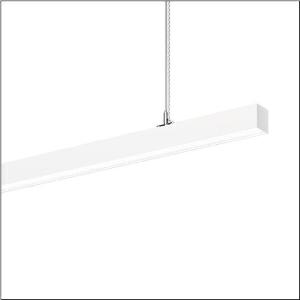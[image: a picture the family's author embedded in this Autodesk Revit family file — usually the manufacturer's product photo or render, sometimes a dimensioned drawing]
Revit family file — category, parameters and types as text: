
# Revit family: silica_r__21_51mx33tctdw_01d4
name_source: partatom
category: Lighting Fixtures
units: mm (PartAtom-declared; Revit-internal decimal feet)

## family parameters
Cut with Voids When Loaded = No
Host = Face
Light Source = No
Part Type = Normal
Room Calculation Point = No
Round Connector Dimension = Use Diameter
Shared = No

## types (1)
- --- (1 x LED, 14340 lm, 134.7 W, 6500K)
    Apparent Load = 135 VA
    CIE Flux Codes = 78 96 99 56 100
    Color Rendering = 80
    Color Temperature = 6500K
    Default Elevation = 1800 mm
    Description = Silica® 21, office luminaire, primary optical cover: prismatic diffuser, of PMMA, CAT 2 (L<= 3000cd/m²), light emission: direct/indirect distribution, primary light characteristic: symmetric, installation type: suspended mounting, LED, rated luminous flux: 14.340lm, luminous efficacy: 101lm/W, light colour: 8tw, colour temperature: 2700..6500K, control gear: ECG DALI, with terminal, 3+2-pole, max. 2.5mm², mains connection: 220..240V, AC, 50/60Hz, rated input power: 141.4W, luminaire housing, of aluminium, traffic white (RAL 9016), length: 3.004mm, width: 53mm, height: 53mm, protection rating (complete): IP20, insulation class (complete): insulation class I (protective earthing), certification: CE, permissible operating ambient temperature: 0..+35°C, standard: EN 50419, packaging unit: 1 piece
    Height = 53 mm
    Lamp = 1 x LED
    Lamp Light Flux = 14340 lm
    Lamp Power = 134.7 W
    Lamp count = 1
    Length = 3004 mm
    Luminous efficacy = 106 lm/W
    Manufacturer = Siteco
    ModVariant = No
    Model = 51MX33TCTDW
    Mounting Place = Ceiling
    Mounting Type = Pendant
    Number of Poles = 1
    OnlyDefault = Yes
    Power Factor = 1
    Product Name = Silica® 21
    Product group = office luminaire | ceiling pendant
    ProductGroupID = 902
    Protection Class = Protection class I
    Protection Degree = IP 20
    RLX_Detail_Level = 1
    RLX_Emergency_Light_Flux = 0 lm
    RLX_Emergency_Type = 0
    RLX_Emergency_Type_DB = No
    RlxData = <blob elided: 18081 chars, md5=bf456bfb>
    Socket = socket
    Standby Power = 0 W
    System Light Flux = 14340 lm
    System Power = 135 W
    Type Comments = individual setting
    Type Image = l_1313629.jpg
    URL = http://relux.com
    VarID = @adj_089139
    Voltage = 0 V
    Weight = 0.00 kg
    Width = 53 mm

## geometry (parser evidence)
native form markers: Blend x4, Sweep x13
no freeform markers — native parametric forms only
